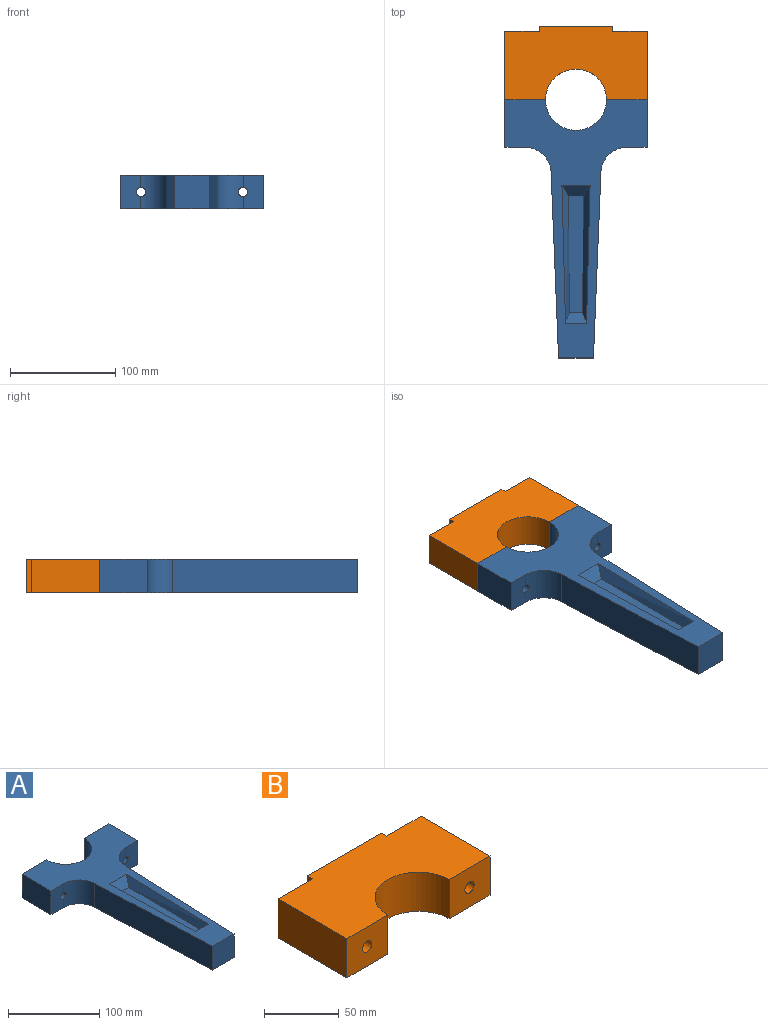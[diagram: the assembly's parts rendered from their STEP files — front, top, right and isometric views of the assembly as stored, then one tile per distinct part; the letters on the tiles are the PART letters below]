
ASSEMBLY  parts=2 mates=1
PART A: 21 faces, bbox 135x245x32 mm
  f0: cylinder r=25mm len=32mm, axis (0,0,1), area 1191mm2, adj f2,f3,f12,f13,f15
  f1: cylinder r=25mm len=32mm, axis (0,0,-1), area 1191mm2, adj f5,f6,f12,f13,f14
  f2: plane 32x18.9mm, normal (0,-1,0), area 577.5mm2, adj f0,f11,f12,f13,f15
  f3: plane 176x32mm, normal (-1,-0.04,0), area 5636.5mm2, adj f0,f4,f12,f13
  f4: plane 33.15x32mm, normal (0,-1,0), area 1060.9mm2, adj f3,f5,f12,f13
  f5: plane 176x32mm, normal (1,-0.04,0), area 5636.5mm2, adj f1,f4,f12,f13
  f6: plane 32x18.9mm, normal (0,-1,0), area 577.5mm2, adj f1,f7,f12,f13,f14
  f7: plane 45x32mm, normal (1,0,0), area 1440mm2, adj f6,f8,f12,f13
  f8: plane 38.5x32mm, normal (0,1,0), area 1171.2mm2, adj f7,f9,f12,f13,f14
  f9: cylinder r=29mm len=58mm, axis (0,0,-1), area 2915.4mm2, adj f8,f10,f12,f13
  f10: plane 38.5x32mm, normal (0,1,0), area 1171.2mm2, adj f9,f11,f12,f13,f15
  f11: plane 45x32mm, normal (-1,0,0), area 1440mm2, adj f2,f10,f12,f13
  f12: plane 245x135mm, normal (0,0,1), area 10169.8mm2, adj f0,f1,f2,f3,f4,f5,f6,f7
  f13: plane 245x135mm, normal (0,0,-1), area 13229mm2, adj f0,f1,f2,f3,f4,f5,f6,f7
  f14: cylinder r=4.4mm len=45.46mm, axis (0,1,0), area 1247.3mm2, adj f1,f6,f8
  f15: cylinder r=4.4mm len=45.46mm, axis (0,1,0), area 1247.3mm2, adj f0,f2,f10
  f16: bspline ~131x10mm, area 1346.4mm2, adj f12,f17,f19,f20
  f17: plane 111x14.79mm, normal (0,0,1), area 1515mm2, adj f16,f18,f19,f20
  f18: bspline ~131x10mm, area 1346.4mm2, adj f12,f17,f19,f20
  f19: plane 20.02x10.02mm, normal (0,0.71,0.71), area 230.6mm2, adj f12,f16,f17,f18
  f20: plane 26.73x10.03mm, normal (0,-0.71,0.71), area 292.7mm2, adj f12,f16,f17,f18
PART B: 14 faces, bbox 135x70x32 mm
  f0: plane 32.5x32mm, normal (0,1,0), area 979.2mm2, adj f1,f9,f10,f11,f12
  f1: plane 32x5mm, normal (1,0,0), area 160mm2, adj f0,f2,f10,f11
  f2: plane 70x32mm, normal (0,1,0), area 2240mm2, adj f1,f3,f10,f11
  f3: plane 32x5mm, normal (-1,0,0), area 160mm2, adj f2,f4,f10,f11
  f4: plane 32.5x32mm, normal (0,1,0), area 979.2mm2, adj f3,f5,f10,f11,f13
  f5: plane 65x32mm, normal (-1,0,0), area 2080mm2, adj f4,f6,f10,f11
  f6: plane 38.5x32mm, normal (0,-1,0), area 1171.2mm2, adj f5,f7,f10,f11,f13
  f7: cylinder r=29mm len=58mm, axis (0,0,-1), area 2915.4mm2, adj f6,f8,f10,f11
  f8: plane 38.5x32mm, normal (0,-1,0), area 1171.2mm2, adj f7,f9,f10,f11,f12
  f9: plane 65x32mm, normal (1,0,0), area 2080mm2, adj f0,f8,f10,f11
  f10: plane 135x70mm, normal (0,0,1), area 7804mm2, adj f0,f1,f2,f3,f4,f5,f6,f7
  f11: plane 135x70mm, normal (0,0,-1), area 7804mm2, adj f0,f1,f2,f3,f4,f5,f6,f7
  f12: cylinder r=4.4mm len=65mm, axis (0,-1,0), area 1797mm2, adj f0,f8
  f13: cylinder r=4.4mm len=65mm, axis (0,-1,0), area 1797mm2, adj f4,f6
PLACE A t=(13.02,-6.24,15.86)mm
PLACE B t=(13.02,-6.24,15.86)mm
MATE fastened A.f15 <-> B.f13  axis (0,1,0) through (-35.23,-6.24,31.86)mm
